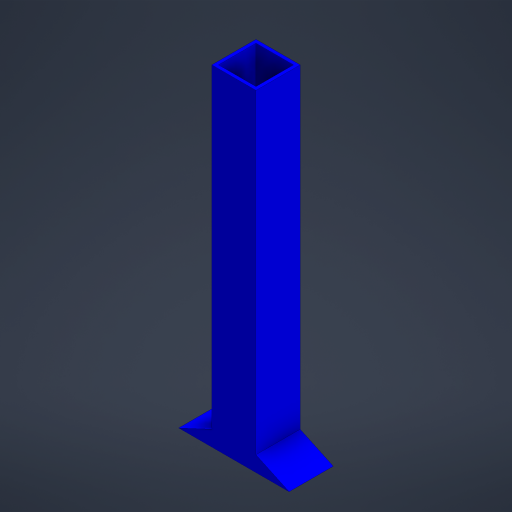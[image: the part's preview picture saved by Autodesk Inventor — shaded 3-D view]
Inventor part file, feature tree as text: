
AUTODESK INVENTOR PART (.ipt)
format: ipt  version: 2024 (Build 280153000, 153)  size: 202,240 bytes
history: native  units: mm
features: other x2, extrude x2, sketch x2, mirror x1
ambient origin geometry x8: Origin, YZ Plane, XZ Plane, XY Plane, X Axis, Y Axis, Z Axis, Center Point
bodies: Body1 (feature_tree)
feature tree (7):
  other  "Твердое тело1"
  extrude  "Выдавливание1"  Depth=20.0mm
  extrude  "Выдавливание2"  Depth=1.5mm
  other  "РабПлоскость1"
  mirror  "Зеркальное отражение1"
  sketch  "Эскиз1"
  sketch  "Эскиз3"
